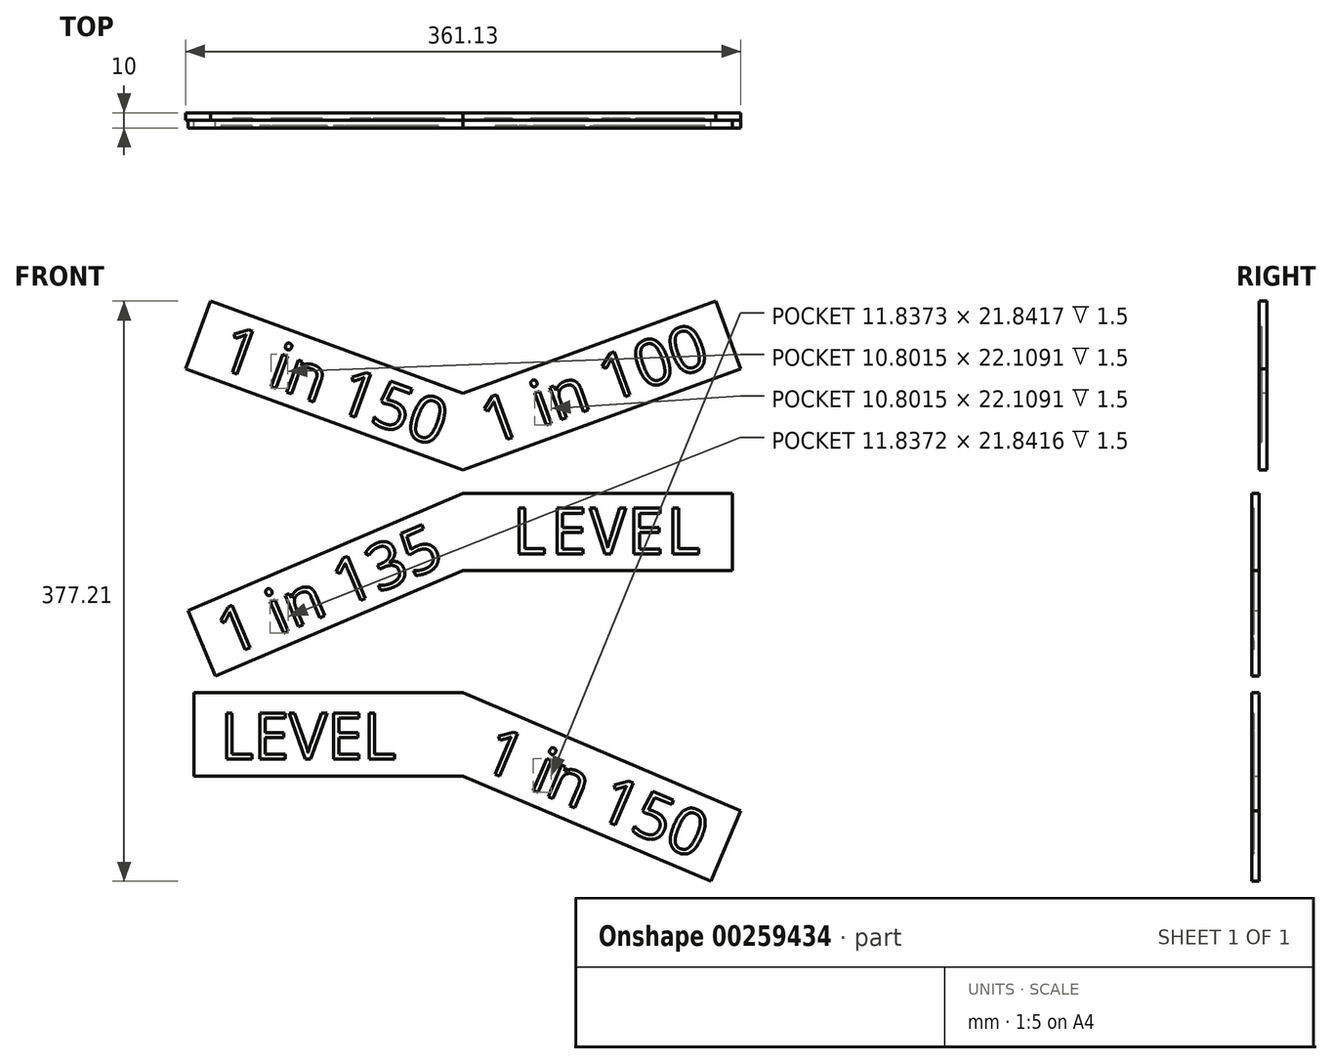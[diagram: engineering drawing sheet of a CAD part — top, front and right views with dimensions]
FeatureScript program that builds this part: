
annotation { "Feature Type Name" : "Feature", "Feature Type Description" : "" }
export const myFeature = defineFeature(function(context is Context, id is Id, definition is map)
    precondition{}
    {
        {
            var Q0;
            Q0=qCreatedBy(makeId("Front.planeOp"),FACE);
            var sketch = newSketch(context, id + "F0", { "sketchPlane" : qUnion([Q0])});
            skLineSegment(sketch, "E0.bottom", {"start": v(0, 0) * mm, "end": v(175, 0) * mm});
            skLineSegment(sketch, "E0.top", {"start": v(0, 50) * mm, "end": v(175, 50) * mm});
            skLineSegment(sketch, "E0.left", {"start": v(0, 0) * mm, "end": v(0, 50) * mm});
            skLineSegment(sketch, "E0.right", {"start": v(175, 0) * mm, "end": v(175, 50) * mm});
            skLineSegment(sketch, "E1", {"start": v(0, 0) * mm, "end": v(-161.04, -68.5) * mm});
            skLineSegment(sketch, "E2", {"start": v(-161.04, -68.5) * mm, "end": v(-179.05, -26.16) * mm});
            skLineSegment(sketch, "E3", {"start": v(0, 50) * mm, "end": v(-179.05, -26.16) * mm});
            skSolve(sketch);
        }
        {
            var Q0;
            Q0 = qSketchRegion(id + "F0", true);
            extrude(context, id + "F1", {"entities" : qUnion([Q0]), "depth" : 5 * mm, "offsetDistance" : 25 * mm});
        }
        {
            var Q0;
            Q0=makeQuery(id+"F1.opExtrude","CAP_FACE",FACE,{"disambiguationData":[OSD([sQuery(id+"F0.wireOp",EDGE,"E0.bottom"),sQuery(id+"F0.wireOp",EDGE,"E0.top"),sQuery(id+"F0.wireOp",EDGE,"E0.right"),sQuery(id+"F0.wireOp",EDGE,"E1"),sQuery(id+"F0.wireOp",EDGE,"E2"),sQuery(id+"F0.wireOp",EDGE,"E3")])],"isStart":false});
            var sketch = newSketch(context, id + "F2", { "sketchPlane" : qUnion([Q0])});
            skText(sketch, "E4", { "text": "LEVEL", "fontName": "DroidSansMono.ttf"});
            skText(sketch, "E5", { "text": "1 in 135", "fontName": "OpenSans-Regular.ttf"});
            const initialGuessF2  = {"E4": [0.03157, 0.01076, 1, 0, 0.03], "E5": [-0.152, -0.05574, 0.92021, 0.39142, 0.03]};
            skSetInitialGuess(sketch, initialGuessF2);
            skSolve(sketch);
        }
        {
            var Q0;
            Q0 = qSketchRegion(id + "F2", true);
            extrude(context, id + "F3", {"entities" : qUnion([Q0]), "operationType" : NewBodyOperationType.REMOVE, "oppositeDirection" : true, "depth" : 1.5 * mm, "offsetDistance" : 25 * mm});
        }
        {
            var Q0;
            Q0=qCreatedBy(makeId("Front.planeOp"),FACE);
            var sketch = newSketch(context, id + "F4", { "sketchPlane" : qUnion([Q0])});
            skLineSegment(sketch, "E6", {"start": v(0, 65.24) * mm, "end": v(0, 115.24) * mm});
            skLineSegment(sketch, "E7", {"start": v(0, 115.24) * mm, "end": v(164.45, 175.1) * mm});
            skLineSegment(sketch, "E8.MirrorCS", {"start": v(0, 115.24) * mm, "end": v(-164.45, 175.1) * mm});
            skLineSegment(sketch, "E9.MirrorCS", {"start": v(-180.52, 130.95) * mm, "end": v(0, 65.24) * mm});
            skLineSegment(sketch, "E10", {"start": v(-164.45, 175.1) * mm, "end": v(-180.52, 130.95) * mm});
            skPoint(sketch, "E11.orphan", {"position": v(-164.45, 125.1) * mm});
            skPoint(sketch, "E12.end.orphan", {"position": v(164.45, 125.1) * mm});
            skLineSegment(sketch, "E13.MirrorCS", {"start": v(164.45, 175.1) * mm, "end": v(180.52, 130.95) * mm});
            skLineSegment(sketch, "E14.MirrorCS", {"start": v(180.52, 130.95) * mm, "end": v(0, 65.24) * mm});
            skSolve(sketch);
        }
        {
            var Q0;
            Q0 = qSketchRegion(id + "F4", true);
            extrude(context, id + "F5", {"entities" : qUnion([Q0]), "oppositeDirection" : true, "depth" : 5 * mm, "offsetDistance" : 25 * mm});
        }
        {
            var Q0;
            Q0=makeQuery(id+"F5.opExtrude","CAP_FACE",FACE,{"disambiguationData":[OSD([sQuery(id+"F4.wireOp",EDGE,"E7"),sQuery(id+"F4.wireOp",EDGE,"E8.MirrorCS"),sQuery(id+"F4.wireOp",EDGE,"E9.MirrorCS"),sQuery(id+"F4.wireOp",EDGE,"E10"),sQuery(id+"F4.wireOp",EDGE,"E13.MirrorCS"),sQuery(id+"F4.wireOp",EDGE,"E14.MirrorCS")])],"isStart":true});
            var sketch = newSketch(context, id + "F6", { "sketchPlane" : qUnion([Q0])});
            skText(sketch, "E15", { "text": "1 in 100", "fontName": "OpenSans-Regular.ttf"});
            skText(sketch, "E16", { "text": "1 in 150", "fontName": "OpenSans-Regular.ttf"});
            const initialGuessF6  = {"E15": [0.01823, 0.08139, 0.9397, 0.34202, 0.03], "E16": [-0.1607, 0.13266, 0.9397, -0.34202, 0.03]};
            skSetInitialGuess(sketch, initialGuessF6);
            skSolve(sketch);
        }
        {
            var Q0;
            Q0 = qSketchRegion(id + "F6", true);
            extrude(context, id + "F7", {"entities" : qUnion([Q0]), "operationType" : NewBodyOperationType.REMOVE, "oppositeDirection" : true, "depth" : 1.5 * mm, "offsetDistance" : 25 * mm});
        }
        {
            var Q0;
            Q0=qCreatedBy(makeId("Front.planeOp"),FACE);
            var sketch = newSketch(context, id + "F8", { "sketchPlane" : qUnion([Q0])});
            skLineSegment(sketch, "E17", {"start": v(0, -79.27) * mm, "end": v(0, -133.6) * mm});
            skLineSegment(sketch, "E18.MirrorCS", {"start": v(180.6, -156.1) * mm, "end": v(0, -79.27) * mm});
            skLineSegment(sketch, "E19.MirrorCS", {"start": v(0, -133.6) * mm, "end": v(161.04, -202.1) * mm});
            skLineSegment(sketch, "E20", {"start": v(0, -133.6) * mm, "end": v(-175, -133.6) * mm});
            skLineSegment(sketch, "E21", {"start": v(-175, -133.6) * mm, "end": v(-175, -79.27) * mm});
            skLineSegment(sketch, "E22", {"start": v(-175, -79.27) * mm, "end": v(0, -79.27) * mm});
            skLineSegment(sketch, "E23", {"start": v(180.6, -156.1) * mm, "end": v(161.04, -202.1) * mm});
            skSolve(sketch);
        }
        {
            var Q0;
            Q0 = qSketchRegion(id + "F8", true);
            extrude(context, id + "F9", {"entities" : qUnion([Q0]), "depth" : 5 * mm, "offsetDistance" : 25 * mm});
        }
        {
            var Q0;
            Q0=makeQuery(id+"F9.opExtrude","CAP_FACE",FACE,{"disambiguationData":[OSD([sQuery(id+"F8.wireOp",EDGE,"E18.MirrorCS"),sQuery(id+"F8.wireOp",EDGE,"E19.MirrorCS"),sQuery(id+"F8.wireOp",EDGE,"E20"),sQuery(id+"F8.wireOp",EDGE,"E21"),sQuery(id+"F8.wireOp",EDGE,"E22"),sQuery(id+"F8.wireOp",EDGE,"E23")])],"isStart":false});
            var sketch = newSketch(context, id + "F10", { "sketchPlane" : qUnion([Q0])});
            skText(sketch, "E24", { "text": "LEVEL", "fontName": "OpenSans-Regular.ttf"});
            skText(sketch, "E25", { "text": "1 in 150", "fontName": "OpenSans-Regular.ttf"});
            const initialGuessF10  = {"E24": [-0.15802, -0.1226, 1, 0, 0.03], "E25": [0.01042, -0.12787, 0.92021, -0.39142, 0.03]};
            skSetInitialGuess(sketch, initialGuessF10);
            skSolve(sketch);
        }
        {
            var Q0;
            Q0 = qSketchRegion(id + "F10", true);
            extrude(context, id + "F11", {"entities" : qUnion([Q0]), "operationType" : NewBodyOperationType.REMOVE, "oppositeDirection" : true, "depth" : 1.5 * mm, "offsetDistance" : 25 * mm});
        }
    });
